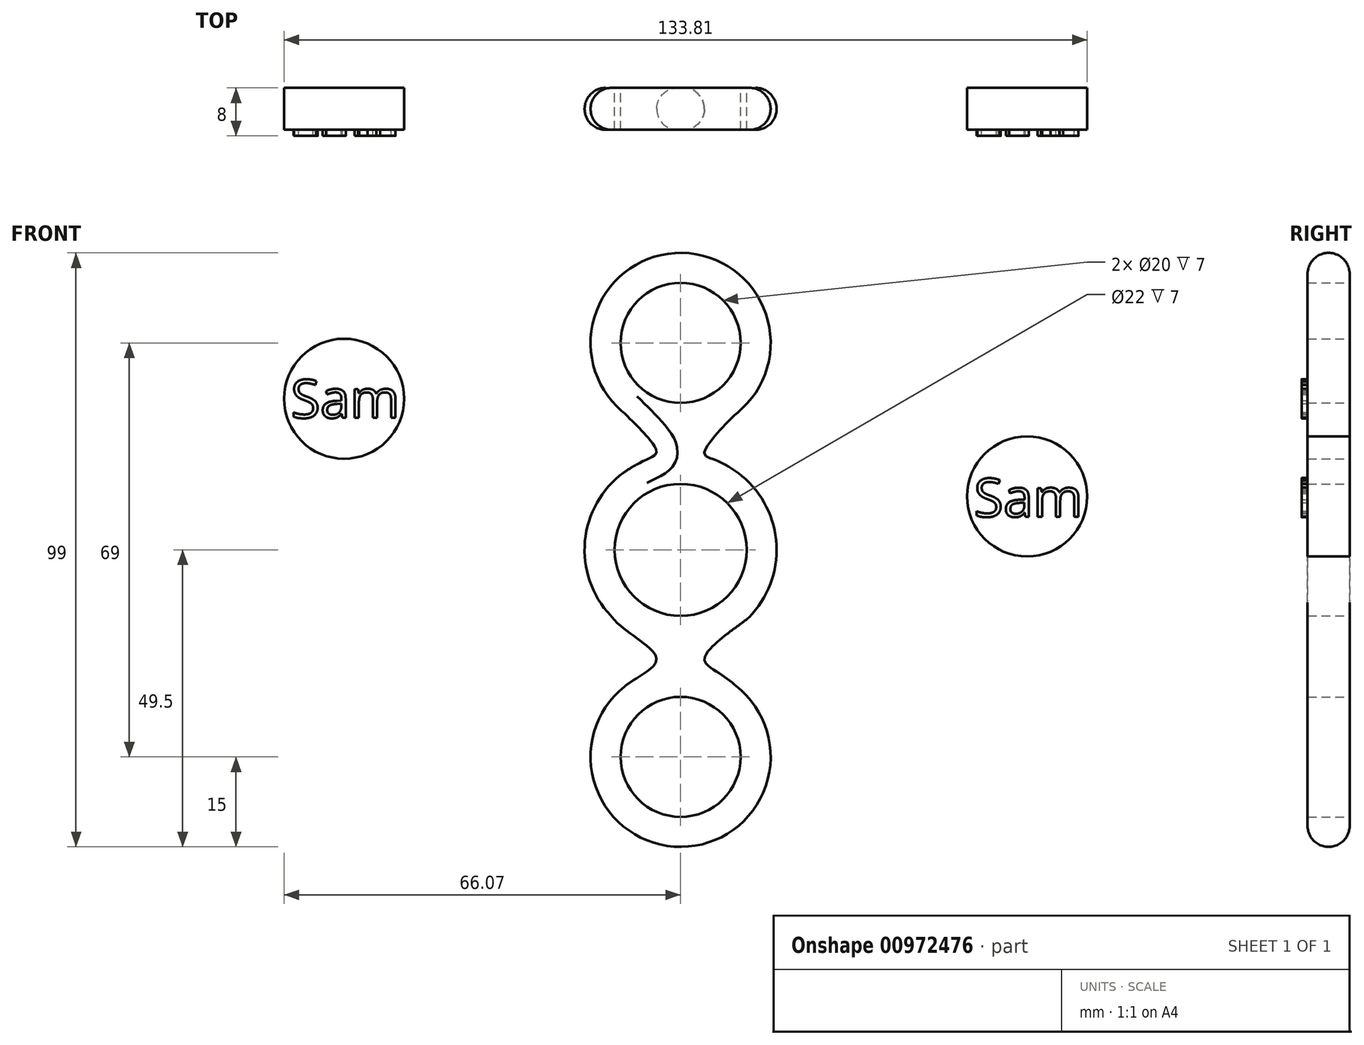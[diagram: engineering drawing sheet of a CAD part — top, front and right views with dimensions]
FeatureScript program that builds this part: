
annotation { "Feature Type Name" : "Feature", "Feature Type Description" : "" }
export const myFeature = defineFeature(function(context is Context, id is Id, definition is map)
    precondition{}
    {
        {
            var Q0;
            Q0=qCreatedBy(makeId("Front.planeOp"),FACE);
            var sketch = newSketch(context, id + "F0", { "sketchPlane" : qUnion([Q0])});
            skCircle(sketch, "E0", {"center": v(0, 0) * mm, "radius": 16 * mm});
            skCircle(sketch, "E1", {"center": v(0, 34.5) * mm, "radius": 15 * mm});
            skFitSpline(sketch, "E2", {"points": [v(10.18, 12.34) * mm, v(4, 16.44) * mm, v(9.38, 22.8) * mm, v(9.72, 23.08) * mm], "startDerivative": vector(-29.15, 23.84) * mm, "endDerivative": vector(0.74, 2.14) * mm});
            skFitSpline(sketch, "E3", {"points": [v(-9.43, 12.93) * mm, v(-4, 16.44) * mm, v(-9.72, 23.08) * mm], "startDerivative": vector(25.98, 17.5) * mm, "endDerivative": vector(-16.44, 15.47) * mm});
            skCircle(sketch, "E4", {"center": v(0, -34.5) * mm, "radius": 15 * mm});
            skFitSpline(sketch, "E5", {"points": [v(-11.56, -11.06) * mm, v(-4, -18.06) * mm, v(-9.34, -22.77) * mm], "startDerivative": vector(10.95, -14.44) * mm, "endDerivative": vector(-15.77, -12.3) * mm});
            skFitSpline(sketch, "E6", {"points": [v(11.2, -11.42) * mm, v(4, -18.06) * mm, v(9.1, -22.58) * mm], "startDerivative": vector(-12.9, -9.93) * mm, "endDerivative": vector(16.4, -15.52) * mm});
            skCircle(sketch, "E7.0", {"center": v(0, -34.5) * mm, "radius": 10 * mm});
            skCircle(sketch, "E8.0", {"center": v(0, 0) * mm, "radius": 11 * mm});
            skCircle(sketch, "E9.0", {"center": v(0, 34.5) * mm, "radius": 10 * mm});
            skSolve(sketch);
        }
        {
            var Q0;
            Q0=makeQuery(id+"F0.imprint","IMPRINT",FACE,{"disambiguationData":[TD([[makeQuery(id+"F0.imprint","IMPRINT",EDGE,{"derivedFrom":sQuery(id+"F0.wireOp",EDGE,"E9.0")}),-1.0]])]});
            var Q1;
            {var subQ0=sQuery(id+"F0.wireOp",EDGE,"E3");Q1=makeQuery(id+"F0.imprint","IMPRINT",FACE,{"disambiguationData":[TD([[makeQuery(id+"F0.imprint","IMPRINT",EDGE,{"derivedFrom":subQ0}),-1.0]])]});}
            var Q2;
            Q2=makeQuery(id+"F0.imprint","IMPRINT",FACE,{"disambiguationData":[TD([[makeQuery(id+"F0.imprint","IMPRINT",EDGE,{"derivedFrom":sQuery(id+"F0.wireOp",EDGE,"E8.0")}),-1.0]])]});
            var Q3;
            {var subQ0=sQuery(id+"F0.wireOp",EDGE,"E5");Q3=makeQuery(id+"F0.imprint","IMPRINT",FACE,{"disambiguationData":[TD([[makeQuery(id+"F0.imprint","IMPRINT",EDGE,{"derivedFrom":subQ0}),1.0]])]});}
            var Q4;
            Q4=makeQuery(id+"F0.imprint","IMPRINT",FACE,{"disambiguationData":[TD([[makeQuery(id+"F0.imprint","IMPRINT",EDGE,{"derivedFrom":sQuery(id+"F0.wireOp",EDGE,"E7.0")}),-1.0]])]});
            extrude(context, id + "F1", {"entities" : qUnion([Q0, Q1, Q2, Q3, Q4]), "depth" : 7 * mm, "offsetDistance" : 25 * mm});
        }
        {
            var Q0;
            Q0=makeQuery(id+"F1.opExtrude","SWEPT_FACE",FACE,{"disambiguationData":[OSD([sQuery(id+"F0.wireOp",EDGE,"E5")])]});
            var Q1;
            Q1=makeQuery(id+"F1.opExtrude","SWEPT_FACE",FACE,{"disambiguationData":[OSD([sQuery(id+"F0.wireOp",EDGE,"E4")])]});
            var Q2;
            Q2=makeQuery(id+"F1.opExtrude","SWEPT_FACE",FACE,{"disambiguationData":[OSD([sQuery(id+"F0.wireOp",EDGE,"E6")])]});
            var Q3;
            {var subQ0=sQuery(id+"F0.wireOp",EDGE,"E2");var subQ1=sQuery(id+"F0.wireOp",EDGE,"E0");var subQ2=makeQuery(id+"F0.imprint","INTERSECT",VERTEX,{"disambiguationData":[OD(0.0)],"derivedFrom":[subQ1,subQ0]});Q3=makeQuery(id+"F1.opExtrude","SWEPT_FACE",FACE,{"disambiguationData":[OSD([subQ1]),TDD([makeQuery(id+"F0.imprint","IMPRINT",EDGE,{"disambiguationData":[TD([[subQ2,-1.0]])],"derivedFrom":subQ1}),makeQuery(id+"F0.imprint","IMPRINT",EDGE,{"disambiguationData":[TD([[subQ2,1.0]])],"derivedFrom":subQ1})])]});}
            var Q4;
            Q4=makeQuery(id+"F1.opExtrude","SWEPT_FACE",FACE,{"disambiguationData":[OSD([sQuery(id+"F0.wireOp",EDGE,"E2")])]});
            var Q5;
            Q5=makeQuery(id+"F1.opExtrude","SWEPT_FACE",FACE,{"disambiguationData":[OSD([sQuery(id+"F0.wireOp",EDGE,"E3")])]});
            var Q6;
            Q6=makeQuery(id+"F1.opExtrude","SWEPT_FACE",FACE,{"disambiguationData":[OSD([sQuery(id+"F0.wireOp",EDGE,"E1")])]});
            var Q7;
            {var subQ0=sQuery(id+"F0.wireOp",EDGE,"E0");Q7=makeQuery(id+"F1.opExtrude","SWEPT_FACE",FACE,{"disambiguationData":[OSD([subQ0]),TDD([makeQuery(id+"F0.imprint","IMPRINT",EDGE,{"disambiguationData":[TD([[makeQuery(id+"F0.imprint","INTERSECT",VERTEX,{"derivedFrom":[subQ0,sQuery(id+"F0.wireOp",EDGE,"E3")]}),-1.0]])],"derivedFrom":subQ0})])]});}
            fillet(context, id + "F2", {"entities" : qUnion([Q0, Q1, Q2, Q3, Q4, Q5, Q6, Q7]), "radius" : 3.5 * mm, "tangentPropagation" : true, "allowEdgeOverflow" : false});
        }
        {
            var Q0;
            Q0=qCreatedBy(makeId("Front.planeOp"),FACE);
            var sketch = newSketch(context, id + "F3", { "sketchPlane" : qUnion([Q0])});
            skCircle(sketch, "E10", {"center": v(70.24, 18.71) * mm, "radius": 10 * mm});
            skSolve(sketch);
        }
        {
            var Q0;
            Q0 = qSketchRegion(id + "F3", true);
            extrude(context, id + "F4", {"entities" : qUnion([Q0]), "depth" : 7 * mm, "offsetDistance" : 25 * mm});
        }
        {
            var Q0;
            Q0=qCreatedBy(makeId("Front.planeOp"),FACE);
            var sketch = newSketch(context, id + "F5", { "sketchPlane" : qUnion([Q0])});
            skCircle(sketch, "E11", {"center": v(-43.57, 34.99) * mm, "radius": 10 * mm});
            skSolve(sketch);
        }
        {
            var Q0;
            Q0 = qSketchRegion(id + "F5", true);
            extrude(context, id + "F6", {"entities" : qUnion([Q0]), "depth" : 7 * mm, "offsetDistance" : 25 * mm});
        }
        {
            var Q0;
            Q0=makeQuery(id+"F6.opExtrude","CAP_FACE",FACE,{"disambiguationData":[OSD([sQuery(id+"F5.wireOp",EDGE,"E11")])],"isStart":false});
            var sketch = newSketch(context, id + "F7", { "sketchPlane" : qUnion([Q0])});
            skText(sketch, "E12", { "text": "Sam", "fontName": "OpenSans-Regular.ttf"});
            const initialGuessF7  = {"E12": [-0.05244, 0.0318, 1, 0, 0.00642]};
            skSetInitialGuess(sketch, initialGuessF7);
            skSolve(sketch);
        }
        {
            var Q0;
            Q0 = qSketchRegion(id + "F7", true);
            extrude(context, id + "F8", {"entities" : qUnion([Q0]), "operationType" : NewBodyOperationType.ADD, "depth" : 1 * mm, "offsetDistance" : 25 * mm});
        }
        {
            var Q0;
            Q0=makeQuery(id+"F4.opExtrude","CAP_FACE",FACE,{"disambiguationData":[OSD([sQuery(id+"F3.wireOp",EDGE,"E10")])],"isStart":false});
            var sketch = newSketch(context, id + "F9", { "sketchPlane" : qUnion([Q0])});
            skText(sketch, "E13", { "text": "Sam", "fontName": "OpenSans-Regular.ttf"});
            const initialGuessF9  = {"E13": [0.06137, 0.01532, 1, 0, 0.00642]};
            skSetInitialGuess(sketch, initialGuessF9);
            skSolve(sketch);
        }
        {
            var Q0;
            Q0 = qSketchRegion(id + "F9", true);
            extrude(context, id + "F10", {"entities" : qUnion([Q0]), "operationType" : NewBodyOperationType.ADD, "depth" : 1 * mm, "offsetDistance" : 25 * mm});
        }
        {
            var Q0;
            Q0=makeQuery(id+"F4.opExtrude","SWEPT_BODY",BODY,{"disambiguationData":[OSD([sQuery(id+"F3.wireOp",EDGE,"E10")])]});
            var Q1;
            Q1=makeQuery(id+"F6.opExtrude","SWEPT_BODY",BODY,{"disambiguationData":[OSD([sQuery(id+"F5.wireOp",EDGE,"E11")])]});
            transform(context, id + "F11", {"entities" : qUnion([Q0, Q1]), "transformType" : TransformType.TRANSLATION_3D, "dx" : -12.5 * mm, "dy" : 0 * mm, "dz" : -9.8 * mm, "makeCopy" : false});
        }
    });
